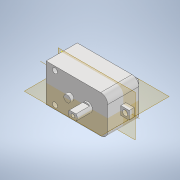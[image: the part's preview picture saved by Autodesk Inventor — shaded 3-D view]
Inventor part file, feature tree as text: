
AUTODESK INVENTOR PART (.ipt)
format: ipt  version: 2022 (Build 260153070, 153G)  size: 163,840 bytes
history: native  units: in
note: dims shown in document units (in); Inventor stores cm internally (conversion verified against a paired STEP export)
features: sketch x6, other x5, plane x2
ambient origin geometry x8: Origin, YZ Plane, XZ Plane, XY Plane, X Axis, Y Axis, Z Axis, Center Point
bodies: Solid1 (feature_tree)
feature tree (13):
  other  "TT motor output.ipt"
  other  "Solid1::TT motor output.ipt"
  other  "TaggingFeature1"
  sketch  "Sketch1"  dims[d0=0.3937in]
  sketch  "Sketch2"
  sketch  "Sketch3"
  sketch  "Sketch4"
  sketch  "Sketch5"
  sketch  "Sketch6"
  plane  "Work Plane1"
  plane  "Work Plane2"
  other  "Work Axis1"
  other  "Work Point1"
